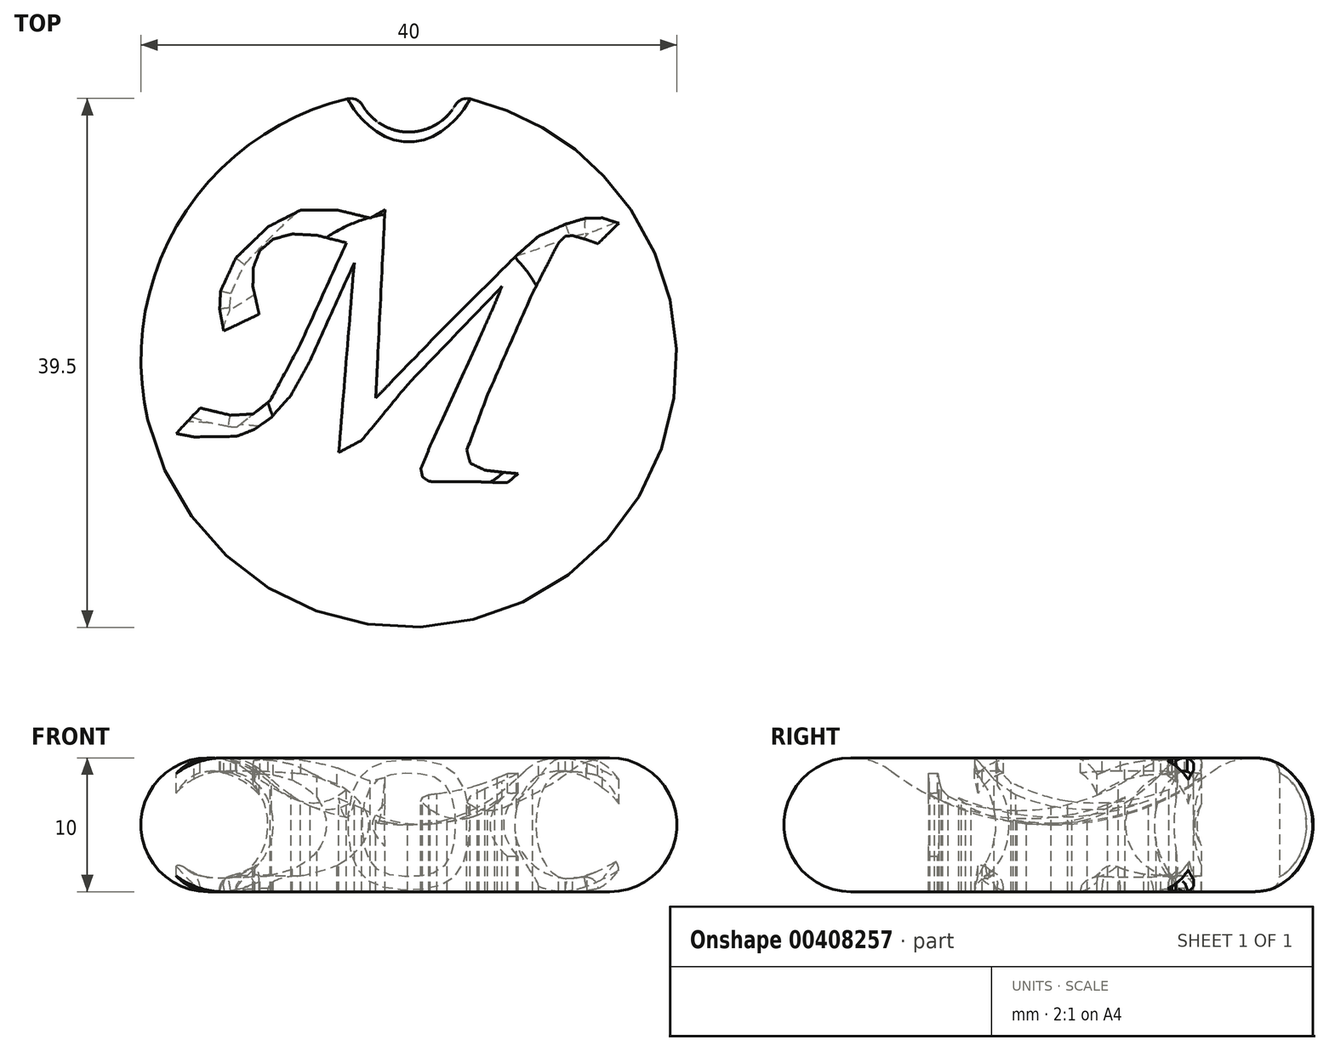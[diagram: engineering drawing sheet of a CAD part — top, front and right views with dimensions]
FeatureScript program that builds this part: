
annotation { "Feature Type Name" : "Feature", "Feature Type Description" : "" }
export const myFeature = defineFeature(function(context is Context, id is Id, definition is map)
    precondition{}
    {
        {
            var Q0;
            Q0=qCreatedBy(makeId("Front.planeOp"),FACE);
            var sketch = newSketch(context, id + "F0", { "sketchPlane" : qUnion([Q0])});
            skArc(sketch, "E0", {"start": v(-12, 9) * mm, "mid": v(-19.74, 6.58) * mm, "end": v(-15, 0) * mm});
            skArc(sketch, "E1", {"start": v(-12, 9) * mm, "mid": v(-6.32, 6.03) * mm, "end": v(0, 5) * mm});
            skLineSegment(sketch, "E2", {"start": v(-15, 0) * mm, "end": v(0, 0) * mm});
            skLineSegment(sketch, "E3", {"start": v(0, 0) * mm, "end": v(0, 5) * mm});
            skSolve(sketch);
        }
        {
            var Q0;
            Q0=makeQuery(id+"F0.imprint","IMPRINT",FACE,{"disambiguationData":[TD([[makeQuery(id+"F0.imprint","IMPRINT",EDGE,{"derivedFrom":sQuery(id+"F0.wireOp",EDGE,"E0")}),1.0]])]});
            var Q1;
            Q1=sQuery(id+"F0.wireOp",EDGE,"E3");
            revolve(context, id + "F1", {"entities" : qUnion([Q0]), "axis" : qUnion([Q1]), "revolveType" : RevolveType.FULL});
        }
        {
            var Q0;
            Q0=qCreatedBy(makeId("Top.planeOp"),FACE);
            cPlane(context, id + "F2", {"entities" : qUnion([Q0]), "cplaneType" : CPlaneType.OFFSET, "offset" : 10 * mm, "width" : 150 * mm, "height" : 150 * mm});
        }
        {
            var Q0;
            Q0=qCreatedBy(id+"F2.planeOp",FACE);
            var sketch = newSketch(context, id + "F3", { "sketchPlane" : qUnion([Q0])});
            skLineSegment(sketch, "E4", {"start": v(8.16, -8.52) * mm, "end": v(6.96, -8.41) * mm});
            skLineSegment(sketch, "E5", {"start": v(6.96, -8.41) * mm, "end": v(5.68, -8.26) * mm});
            skLineSegment(sketch, "E6", {"start": v(5.68, -8.26) * mm, "end": v(4.58, -7.74) * mm});
            skLineSegment(sketch, "E7", {"start": v(4.58, -7.74) * mm, "end": v(4.33, -6.76) * mm});
            skLineSegment(sketch, "E8", {"start": v(4.33, -6.76) * mm, "end": v(5.89, -2.6) * mm});
            skLineSegment(sketch, "E9", {"start": v(5.89, -2.6) * mm, "end": v(9.23, 4.96) * mm});
            skLineSegment(sketch, "E10", {"start": v(9.23, 4.96) * mm, "end": v(11.16, 8.7) * mm});
            skLineSegment(sketch, "E11", {"start": v(11.16, 8.7) * mm, "end": v(11.7, 9.22) * mm});
            skLineSegment(sketch, "E12", {"start": v(11.7, 9.22) * mm, "end": v(12.22, 9.26) * mm});
            skLineSegment(sketch, "E13", {"start": v(12.22, 9.26) * mm, "end": v(13.3, 8.95) * mm});
            skLineSegment(sketch, "E14", {"start": v(13.3, 8.95) * mm, "end": v(14.1, 8.65) * mm});
            skLineSegment(sketch, "E15", {"start": v(14.1, 8.65) * mm, "end": v(15.67, 10.18) * mm});
            skLineSegment(sketch, "E16", {"start": v(15.67, 10.18) * mm, "end": v(14.46, 10.58) * mm});
            skLineSegment(sketch, "E17", {"start": v(14.46, 10.58) * mm, "end": v(13.23, 10.57) * mm});
            skLineSegment(sketch, "E18", {"start": v(13.23, 10.57) * mm, "end": v(11.7, 10.11) * mm});
            skLineSegment(sketch, "E19", {"start": v(11.7, 10.11) * mm, "end": v(9.67, 9.2) * mm});
            skLineSegment(sketch, "E20", {"start": v(9.67, 9.2) * mm, "end": v(8.04, 7.78) * mm});
            skLineSegment(sketch, "E21", {"start": v(8.04, 7.78) * mm, "end": v(2.86, 2.64) * mm});
            skLineSegment(sketch, "E22", {"start": v(2.86, 2.64) * mm, "end": v(-1.5, -1.88) * mm});
            skLineSegment(sketch, "E23", {"start": v(-1.5, -1.88) * mm, "end": v(-2.47, -2.87) * mm});
            skLineSegment(sketch, "E24", {"start": v(-2.47, -2.87) * mm, "end": v(-1.78, 11.19) * mm});
            skLineSegment(sketch, "E25", {"start": v(-1.78, 11.19) * mm, "end": v(-2.88, 10.57) * mm});
            skLineSegment(sketch, "E26", {"start": v(-2.88, 10.57) * mm, "end": v(-5.37, 11.18) * mm});
            skLineSegment(sketch, "E27", {"start": v(-5.37, 11.18) * mm, "end": v(-8.07, 11.16) * mm});
            skLineSegment(sketch, "E28", {"start": v(-8.07, 11.16) * mm, "end": v(-10.5, 9.93) * mm});
            skLineSegment(sketch, "E29", {"start": v(-10.5, 9.93) * mm, "end": v(-12.92, 7.6) * mm});
            skLineSegment(sketch, "E30", {"start": v(-12.92, 7.6) * mm, "end": v(-14.06, 5.12) * mm});
            skLineSegment(sketch, "E31", {"start": v(-14.06, 5.12) * mm, "end": v(-14.12, 3.75) * mm});
            skLineSegment(sketch, "E32", {"start": v(-14.12, 3.75) * mm, "end": v(-13.82, 2.13) * mm});
            skLineSegment(sketch, "E33", {"start": v(-13.82, 2.13) * mm, "end": v(-11.18, 3.39) * mm});
            skLineSegment(sketch, "E34", {"start": v(-11.18, 3.39) * mm, "end": v(-11.64, 5.43) * mm});
            skLineSegment(sketch, "E35", {"start": v(-11.64, 5.43) * mm, "end": v(-11.63, 6.85) * mm});
            skLineSegment(sketch, "E36", {"start": v(-11.63, 6.85) * mm, "end": v(-11.12, 8.15) * mm});
            skLineSegment(sketch, "E37", {"start": v(-11.12, 8.15) * mm, "end": v(-10.13, 9) * mm});
            skLineSegment(sketch, "E38", {"start": v(-10.13, 9) * mm, "end": v(-8.7, 9.38) * mm});
            skLineSegment(sketch, "E39", {"start": v(-8.7, 9.38) * mm, "end": v(-6.87, 9.29) * mm});
            skLineSegment(sketch, "E40", {"start": v(-6.87, 9.29) * mm, "end": v(-4.66, 8.72) * mm});
            skLineSegment(sketch, "E41", {"start": v(-4.66, 8.72) * mm, "end": v(-8.1, 1.17) * mm});
            skLineSegment(sketch, "E42", {"start": v(-8.1, 1.17) * mm, "end": v(-10.34, -3.06) * mm});
            skLineSegment(sketch, "E43", {"start": v(-10.34, -3.06) * mm, "end": v(-11.61, -4.06) * mm});
            skLineSegment(sketch, "E44", {"start": v(-11.61, -4.06) * mm, "end": v(-13.3, -4.16) * mm});
            skLineSegment(sketch, "E45", {"start": v(-13.3, -4.16) * mm, "end": v(-15.58, -3.62) * mm});
            skLineSegment(sketch, "E46", {"start": v(-15.58, -3.62) * mm, "end": v(-17.37, -5.52) * mm});
            skLineSegment(sketch, "E47", {"start": v(-17.37, -5.52) * mm, "end": v(-16.04, -5.78) * mm});
            skLineSegment(sketch, "E48", {"start": v(-16.04, -5.78) * mm, "end": v(-12.85, -5.73) * mm});
            skLineSegment(sketch, "E49", {"start": v(-12.85, -5.73) * mm, "end": v(-11.5, -5.2) * mm});
            skLineSegment(sketch, "E50", {"start": v(-11.5, -5.2) * mm, "end": v(-10.26, -4.32) * mm});
            skLineSegment(sketch, "E51", {"start": v(-10.26, -4.32) * mm, "end": v(-8.8, -2.68) * mm});
            skLineSegment(sketch, "E52", {"start": v(-8.8, -2.68) * mm, "end": v(-7.38, -0.06) * mm});
            skLineSegment(sketch, "E53", {"start": v(-7.38, -0.06) * mm, "end": v(-4.08, 7.22) * mm});
            skLineSegment(sketch, "E54", {"start": v(-4.08, 7.22) * mm, "end": v(-5.23, -6.95) * mm});
            skLineSegment(sketch, "E55", {"start": v(-5.23, -6.95) * mm, "end": v(-3.51, -6.02) * mm});
            skLineSegment(sketch, "E56", {"start": v(-3.51, -6.02) * mm, "end": v(-0.11, -1.89) * mm});
            skLineSegment(sketch, "E57", {"start": v(-0.11, -1.89) * mm, "end": v(6.95, 5.47) * mm});
            skLineSegment(sketch, "E58", {"start": v(6.95, 5.47) * mm, "end": v(6.41, 4.15) * mm});
            skLineSegment(sketch, "E59", {"start": v(6.41, 4.15) * mm, "end": v(5.23, 1.5) * mm});
            skLineSegment(sketch, "E60", {"start": v(5.23, 1.5) * mm, "end": v(1.6, -6.43) * mm});
            skLineSegment(sketch, "E61", {"start": v(1.6, -6.43) * mm, "end": v(0.9, -8.17) * mm});
            skLineSegment(sketch, "E62", {"start": v(0.9, -8.17) * mm, "end": v(1.02, -8.77) * mm});
            skLineSegment(sketch, "E63", {"start": v(1.02, -8.77) * mm, "end": v(1.5, -9.1) * mm});
            skLineSegment(sketch, "E64", {"start": v(1.5, -9.1) * mm, "end": v(2.1, -9.14) * mm});
            skLineSegment(sketch, "E65", {"start": v(2.1, -9.14) * mm, "end": v(5.12, -9.13) * mm});
            skLineSegment(sketch, "E66", {"start": v(5.12, -9.13) * mm, "end": v(6.6, -9.19) * mm});
            skLineSegment(sketch, "E67", {"start": v(6.6, -9.19) * mm, "end": v(7.38, -9.19) * mm});
            skLineSegment(sketch, "E68", {"start": v(7.38, -9.19) * mm, "end": v(8.16, -8.52) * mm});
            skSolve(sketch);
        }
        {
            var Q0;
            Q0=makeQuery(id+"F3.imprint","IMPRINT",FACE,{"disambiguationData":[TD([[makeQuery(id+"F3.imprint","IMPRINT",EDGE,{"derivedFrom":sQuery(id+"F3.wireOp",EDGE,"E4")}),1.0]])]});
            extrude(context, id + "F4", {"entities" : qUnion([Q0]), "operationType" : NewBodyOperationType.REMOVE, "oppositeDirection" : true, "depth" : 25 * mm});
        }
        {
            var Q0;
            Q0=qCreatedBy(makeId("Front.planeOp"),FACE);
            var sketch = newSketch(context, id + "F5", { "sketchPlane" : qUnion([Q0])});
            skCircle(sketch, "E69", {"center": v(-15, 5) * mm, "radius": 4 * mm});
            skSolve(sketch);
        }
        {
            var Q0;
            Q0 = qSketchRegion(id + "F5", true);
            var Q1;
            Q1=sQuery(id+"F0.wireOp",EDGE,"E3");
            revolve(context, id + "F6", {"operationType" : NewBodyOperationType.ADD, "entities" : qUnion([Q0]), "axis" : qUnion([Q1]), "revolveType" : RevolveType.FULL});
        }
        {
            var Q0;
            Q0=qCreatedBy(makeId("Top.planeOp"),FACE);
            var sketch = newSketch(context, id + "F7", { "sketchPlane" : qUnion([Q0])});
            skCircle(sketch, "E70", {"center": v(0, 21) * mm, "radius": 4 * mm});
            skSolve(sketch);
        }
        {
            var Q0;
            Q0=makeQuery(id+"F7.imprint","IMPRINT",FACE,{"disambiguationData":[TD([[makeQuery(id+"F7.imprint","IMPRINT",EDGE,{"derivedFrom":sQuery(id+"F7.wireOp",EDGE,"E70")}),1.0]])]});
            extrude(context, id + "F8", {"entities" : qUnion([Q0]), "operationType" : NewBodyOperationType.REMOVE, "depth" : 25 * mm});
        }
        {
            var Q0;
            Q0=makeQuery(id+"F8.boolean.opBoolean","INTERSECT",EDGE,{"derivedFrom":[makeQuery(id+"F4.boolean.opBoolean","SPLIT",FACE,{"disambiguationData":[TD([makeQuery(id+"F1.opRevolve","SWEPT_FACE",FACE,{"disambiguationData":[OSD([sQuery(id+"F0.wireOp",EDGE,"E2")])]})])],"derivedFrom":makeQuery(id+"F1.opRevolve","SWEPT_FACE",FACE,{"disambiguationData":[OSD([sQuery(id+"F0.wireOp",EDGE,"E0")])]})}),makeQuery(id+"F8.opExtrude","SWEPT_FACE",FACE,{"disambiguationData":[OSD([sQuery(id+"F7.wireOp",EDGE,"E70")])]})]});
            fillet(context, id + "F9", {"entities" : qUnion([Q0]), "radius" : 1 * mm, "tangentPropagation" : true, "allowEdgeOverflow" : false});
        }
        {
            var Q0;
            Q0=makeQuery(id+"F6.boolean.opBoolean","INTERSECT",EDGE,{"disambiguationData":[OD(0.0)],"derivedFrom":[makeQuery(id+"F4.boolean.opBoolean","COPY",FACE,{"derivedFrom":makeQuery(id+"F4.opExtrude","SWEPT_FACE",FACE,{"disambiguationData":[OSD([sQuery(id+"F3.wireOp",EDGE,"E48")])]})}),makeQuery(id+"F6.opRevolve","SWEPT_FACE",FACE,{"disambiguationData":[OSD([sQuery(id+"F5.wireOp",EDGE,"E69")])]})]});
            fillet(context, id + "F10", {"entities" : qUnion([Q0]), "radius" : 1 * mm, "tangentPropagation" : true, "allowEdgeOverflow" : false});
        }
        {
            var Q0;
            Q0=makeQuery(id+"F6.boolean.opBoolean","INTERSECT",EDGE,{"disambiguationData":[OD(0.0)],"derivedFrom":[makeQuery(id+"F4.boolean.opBoolean","COPY",FACE,{"derivedFrom":makeQuery(id+"F4.opExtrude","SWEPT_FACE",FACE,{"disambiguationData":[OSD([sQuery(id+"F3.wireOp",EDGE,"E45")])]})}),makeQuery(id+"F6.opRevolve","SWEPT_FACE",FACE,{"disambiguationData":[OSD([sQuery(id+"F5.wireOp",EDGE,"E69")])]})]});
            fillet(context, id + "F11", {"entities" : qUnion([Q0]), "radius" : 1 * mm, "tangentPropagation" : true, "allowEdgeOverflow" : false});
        }
        {
            var Q0;
            Q0=makeQuery(id+"F6.boolean.opBoolean","INTERSECT",EDGE,{"disambiguationData":[OD(1.0)],"derivedFrom":[makeQuery(id+"F4.boolean.opBoolean","COPY",FACE,{"derivedFrom":makeQuery(id+"F4.opExtrude","SWEPT_FACE",FACE,{"disambiguationData":[OSD([sQuery(id+"F3.wireOp",EDGE,"E44")])]})}),makeQuery(id+"F6.opRevolve","SWEPT_FACE",FACE,{"disambiguationData":[OSD([sQuery(id+"F5.wireOp",EDGE,"E69")])]})]});
            fillet(context, id + "F12", {"entities" : qUnion([Q0]), "radius" : 1 * mm, "tangentPropagation" : true, "allowEdgeOverflow" : false});
        }
        {
            var Q0;
            Q0=makeQuery(id+"F6.boolean.opBoolean","INTERSECT",EDGE,{"disambiguationData":[OD(1.0)],"derivedFrom":[makeQuery(id+"F4.boolean.opBoolean","COPY",FACE,{"derivedFrom":makeQuery(id+"F4.opExtrude","SWEPT_FACE",FACE,{"disambiguationData":[OSD([sQuery(id+"F3.wireOp",EDGE,"E32")])]})}),makeQuery(id+"F6.opRevolve","SWEPT_FACE",FACE,{"disambiguationData":[OSD([sQuery(id+"F5.wireOp",EDGE,"E69")])]})]});
            var Q1;
            Q1=makeQuery(id+"F6.boolean.opBoolean","INTERSECT",EDGE,{"disambiguationData":[OD(1.0)],"derivedFrom":[makeQuery(id+"F4.boolean.opBoolean","COPY",FACE,{"derivedFrom":makeQuery(id+"F4.opExtrude","SWEPT_FACE",FACE,{"disambiguationData":[OSD([sQuery(id+"F3.wireOp",EDGE,"E31")])]})}),makeQuery(id+"F6.opRevolve","SWEPT_FACE",FACE,{"disambiguationData":[OSD([sQuery(id+"F5.wireOp",EDGE,"E69")])]})]});
            var Q2;
            Q2=makeQuery(id+"F6.boolean.opBoolean","INTERSECT",EDGE,{"disambiguationData":[OD(1.0)],"derivedFrom":[makeQuery(id+"F4.boolean.opBoolean","COPY",FACE,{"derivedFrom":makeQuery(id+"F4.opExtrude","SWEPT_FACE",FACE,{"disambiguationData":[OSD([sQuery(id+"F3.wireOp",EDGE,"E30")])]})}),makeQuery(id+"F6.opRevolve","SWEPT_FACE",FACE,{"disambiguationData":[OSD([sQuery(id+"F5.wireOp",EDGE,"E69")])]})]});
            var Q3;
            Q3=makeQuery(id+"F6.boolean.opBoolean","INTERSECT",EDGE,{"disambiguationData":[OD(1.0)],"derivedFrom":[makeQuery(id+"F4.boolean.opBoolean","COPY",FACE,{"derivedFrom":makeQuery(id+"F4.opExtrude","SWEPT_FACE",FACE,{"disambiguationData":[OSD([sQuery(id+"F3.wireOp",EDGE,"E29")])]})}),makeQuery(id+"F6.opRevolve","SWEPT_FACE",FACE,{"disambiguationData":[OSD([sQuery(id+"F5.wireOp",EDGE,"E69")])]})]});
            var Q4;
            Q4=makeQuery(id+"F6.boolean.opBoolean","INTERSECT",EDGE,{"disambiguationData":[OD(1.0)],"derivedFrom":[makeQuery(id+"F4.boolean.opBoolean","COPY",FACE,{"derivedFrom":makeQuery(id+"F4.opExtrude","SWEPT_FACE",FACE,{"disambiguationData":[OSD([sQuery(id+"F3.wireOp",EDGE,"E33")])]})}),makeQuery(id+"F6.opRevolve","SWEPT_FACE",FACE,{"disambiguationData":[OSD([sQuery(id+"F5.wireOp",EDGE,"E69")])]})]});
            fillet(context, id + "F13", {"entities" : qUnion([Q0, Q1, Q2, Q3, Q4]), "radius" : 1 * mm, "tangentPropagation" : true, "allowEdgeOverflow" : false});
        }
        {
            var Q0;
            Q0=makeQuery(id+"F6.boolean.opBoolean","INTERSECT",EDGE,{"disambiguationData":[OD(0.0)],"derivedFrom":[makeQuery(id+"F4.boolean.opBoolean","COPY",FACE,{"derivedFrom":makeQuery(id+"F4.opExtrude","SWEPT_FACE",FACE,{"disambiguationData":[OSD([sQuery(id+"F3.wireOp",EDGE,"E15")])]})}),makeQuery(id+"F6.opRevolve","SWEPT_FACE",FACE,{"disambiguationData":[OSD([sQuery(id+"F5.wireOp",EDGE,"E69")])]})]});
            fillet(context, id + "F14", {"entities" : qUnion([Q0]), "radius" : 1 * mm, "tangentPropagation" : true, "allowEdgeOverflow" : false});
        }
        {
            var Q0;
            Q0=makeQuery(id+"F6.boolean.opBoolean","INTERSECT",EDGE,{"disambiguationData":[OD(0.0)],"derivedFrom":[makeQuery(id+"F4.boolean.opBoolean","COPY",FACE,{"derivedFrom":makeQuery(id+"F4.opExtrude","SWEPT_FACE",FACE,{"disambiguationData":[OSD([sQuery(id+"F3.wireOp",EDGE,"E19")])]})}),makeQuery(id+"F6.opRevolve","SWEPT_FACE",FACE,{"disambiguationData":[OSD([sQuery(id+"F5.wireOp",EDGE,"E69")])]})]});
            var Q1;
            Q1=makeQuery(id+"F6.boolean.opBoolean","INTERSECT",EDGE,{"disambiguationData":[OD(0.0)],"derivedFrom":[makeQuery(id+"F4.boolean.opBoolean","COPY",FACE,{"derivedFrom":makeQuery(id+"F4.opExtrude","SWEPT_FACE",FACE,{"disambiguationData":[OSD([sQuery(id+"F3.wireOp",EDGE,"E18")])]})}),makeQuery(id+"F6.opRevolve","SWEPT_FACE",FACE,{"disambiguationData":[OSD([sQuery(id+"F5.wireOp",EDGE,"E69")])]})]});
            var Q2;
            Q2=makeQuery(id+"F6.boolean.opBoolean","INTERSECT",EDGE,{"disambiguationData":[OD(0.0)],"derivedFrom":[makeQuery(id+"F4.boolean.opBoolean","COPY",FACE,{"derivedFrom":makeQuery(id+"F4.opExtrude","SWEPT_FACE",FACE,{"disambiguationData":[OSD([sQuery(id+"F3.wireOp",EDGE,"E17")])]})}),makeQuery(id+"F6.opRevolve","SWEPT_FACE",FACE,{"disambiguationData":[OSD([sQuery(id+"F5.wireOp",EDGE,"E69")])]})]});
            fillet(context, id + "F15", {"entities" : qUnion([Q0, Q1, Q2]), "radius" : 1 * mm, "tangentPropagation" : true, "allowEdgeOverflow" : false});
        }
    });
